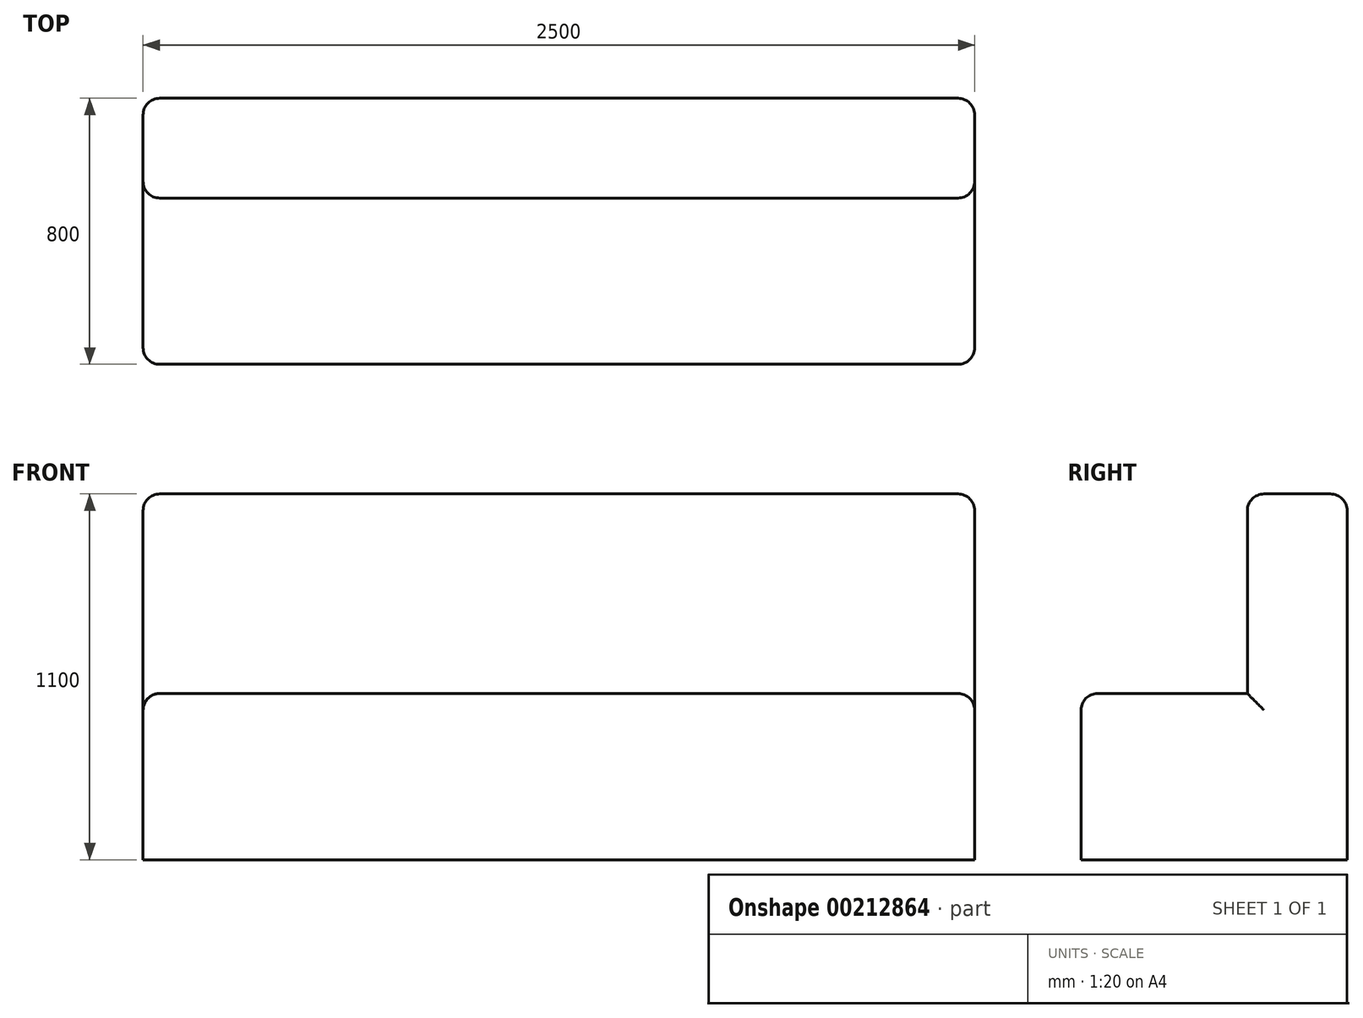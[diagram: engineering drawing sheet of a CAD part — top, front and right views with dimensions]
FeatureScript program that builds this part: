
annotation { "Feature Type Name" : "Feature", "Feature Type Description" : "" }
export const myFeature = defineFeature(function(context is Context, id is Id, definition is map)
    precondition{}
    {
        {
            var Q0;
            Q0=qCreatedBy(makeId("Top.planeOp"),FACE);
            var sketch = newSketch(context, id + "F0", { "sketchPlane" : qUnion([Q0])});
            skLineSegment(sketch, "E0.bottom", {"start": v(0, 0) * mm, "end": v(2500, 0) * mm});
            skLineSegment(sketch, "E0.top", {"start": v(0, 800) * mm, "end": v(2500, 800) * mm});
            skLineSegment(sketch, "E0.left", {"start": v(0, 0) * mm, "end": v(0, 800) * mm});
            skLineSegment(sketch, "E0.right", {"start": v(2500, 0) * mm, "end": v(2500, 800) * mm});
            skSolve(sketch);
        }
        {
            var Q0;
            Q0 = qSketchRegion(id + "F0", true);
            extrude(context, id + "F1", {"entities" : qUnion([Q0]), "depth" : 500 * mm});
        }
        {
            var Q0;
            Q0=makeQuery(id+"F1.opExtrude","CAP_FACE",FACE,{"disambiguationData":[OSD([sQuery(id+"F0.wireOp",EDGE,"E0.bottom"),sQuery(id+"F0.wireOp",EDGE,"E0.top"),sQuery(id+"F0.wireOp",EDGE,"E0.left"),sQuery(id+"F0.wireOp",EDGE,"E0.right")])],"isStart":false});
            var sketch = newSketch(context, id + "F2", { "sketchPlane" : qUnion([Q0])});
            skLineSegment(sketch, "E1.bottom", {"start": v(0, 800) * mm, "end": v(2500, 800) * mm});
            skLineSegment(sketch, "E1.top", {"start": v(0, 500) * mm, "end": v(2500, 500) * mm});
            skLineSegment(sketch, "E1.left", {"start": v(0, 800) * mm, "end": v(0, 500) * mm});
            skLineSegment(sketch, "E1.right", {"start": v(2500, 800) * mm, "end": v(2500, 500) * mm});
            skSolve(sketch);
        }
        {
            var Q0;
            Q0 = qSketchRegion(id + "F2", true);
            extrude(context, id + "F3", {"entities" : qUnion([Q0]), "operationType" : NewBodyOperationType.ADD, "depth" : 600 * mm});
        }
        {
            var Q0;
            Q0=makeQuery(id+"F3.opExtrude","CAP_EDGE",EDGE,{"disambiguationData":[OSD([sQuery(id+"F2.wireOp",EDGE,"E1.top")])],"isStart":true});
            var Q1;
            Q1=makeQuery(id+"F1.opExtrude","CAP_EDGE",EDGE,{"disambiguationData":[OSD([sQuery(id+"F0.wireOp",EDGE,"E0.bottom")])],"isStart":false});
            var Q2;
            Q2=makeQuery(id+"F1.opExtrude","SWEPT_EDGE",EDGE,{"disambiguationData":[OSD([sQuery(id+"F0.wireOp",EDGE,"E0.bottom"),sQuery(id+"F0.wireOp",EDGE,"E0.left")])]});
            var Q3;
            Q3=makeQuery(id+"F1.opExtrude","CAP_EDGE",EDGE,{"disambiguationData":[OSD([sQuery(id+"F0.wireOp",EDGE,"E0.left")])],"isStart":false});
            var Q4;
            Q4=makeQuery(id+"F3.boolean.opBoolean","MERGE",EDGE,{"derivedFrom":[makeQuery(id+"F1.opExtrude","SWEPT_EDGE",EDGE,{"disambiguationData":[OSD([sQuery(id+"F0.wireOp",EDGE,"E0.top"),sQuery(id+"F0.wireOp",EDGE,"E0.left")])]}),makeQuery(id+"F3.opExtrude","SWEPT_EDGE",EDGE,{"disambiguationData":[OSD([sQuery(id+"F2.wireOp",EDGE,"E1.bottom"),sQuery(id+"F2.wireOp",EDGE,"E1.left")])]})]});
            var Q5;
            Q5=makeQuery(id+"F3.opExtrude","CAP_EDGE",EDGE,{"disambiguationData":[OSD([sQuery(id+"F2.wireOp",EDGE,"E1.top")])],"isStart":false});
            var Q6;
            Q6=makeQuery(id+"F3.opExtrude","CAP_EDGE",EDGE,{"disambiguationData":[OSD([sQuery(id+"F2.wireOp",EDGE,"E1.bottom")])],"isStart":false});
            var Q7;
            Q7=makeQuery(id+"F3.opExtrude","SWEPT_EDGE",EDGE,{"disambiguationData":[OSD([sQuery(id+"F0.wireOp",EDGE,"E0.right"),sQuery(id+"F2.wireOp",EDGE,"E1.top"),sQuery(id+"F2.wireOp",EDGE,"E1.right")])]});
            var Q8;
            Q8=makeQuery(id+"F1.opExtrude","CAP_EDGE",EDGE,{"disambiguationData":[OSD([sQuery(id+"F0.wireOp",EDGE,"E0.right")])],"isStart":false});
            var Q9;
            Q9=makeQuery(id+"F1.opExtrude","SWEPT_EDGE",EDGE,{"disambiguationData":[OSD([sQuery(id+"F0.wireOp",EDGE,"E0.bottom"),sQuery(id+"F0.wireOp",EDGE,"E0.right")])]});
            var Q10;
            Q10=makeQuery(id+"F3.boolean.opBoolean","MERGE",EDGE,{"derivedFrom":[makeQuery(id+"F1.opExtrude","SWEPT_EDGE",EDGE,{"disambiguationData":[OSD([sQuery(id+"F0.wireOp",EDGE,"E0.top"),sQuery(id+"F0.wireOp",EDGE,"E0.right")])]}),makeQuery(id+"F3.opExtrude","SWEPT_EDGE",EDGE,{"disambiguationData":[OSD([sQuery(id+"F2.wireOp",EDGE,"E1.bottom"),sQuery(id+"F2.wireOp",EDGE,"E1.right")])]})]});
            var Q11;
            Q11=makeQuery(id+"F3.opExtrude","CAP_EDGE",EDGE,{"disambiguationData":[OSD([sQuery(id+"F2.wireOp",EDGE,"E1.right")])],"isStart":false});
            var Q12;
            Q12=makeQuery(id+"F3.opExtrude","CAP_EDGE",EDGE,{"disambiguationData":[OSD([sQuery(id+"F2.wireOp",EDGE,"E1.left")])],"isStart":false});
            var Q13;
            Q13=makeQuery(id+"F3.opExtrude","SWEPT_EDGE",EDGE,{"disambiguationData":[OSD([sQuery(id+"F0.wireOp",EDGE,"E0.left"),sQuery(id+"F2.wireOp",EDGE,"E1.top"),sQuery(id+"F2.wireOp",EDGE,"E1.left")])]});
            fillet(context, id + "F4", {"entities" : qUnion([Q0, Q1, Q2, Q3, Q4, Q5, Q6, Q7, Q8, Q9, Q10, Q11, Q12, Q13]), "radius" : 50 * mm, "tangentPropagation" : true, "allowEdgeOverflow" : false});
        }
    });
